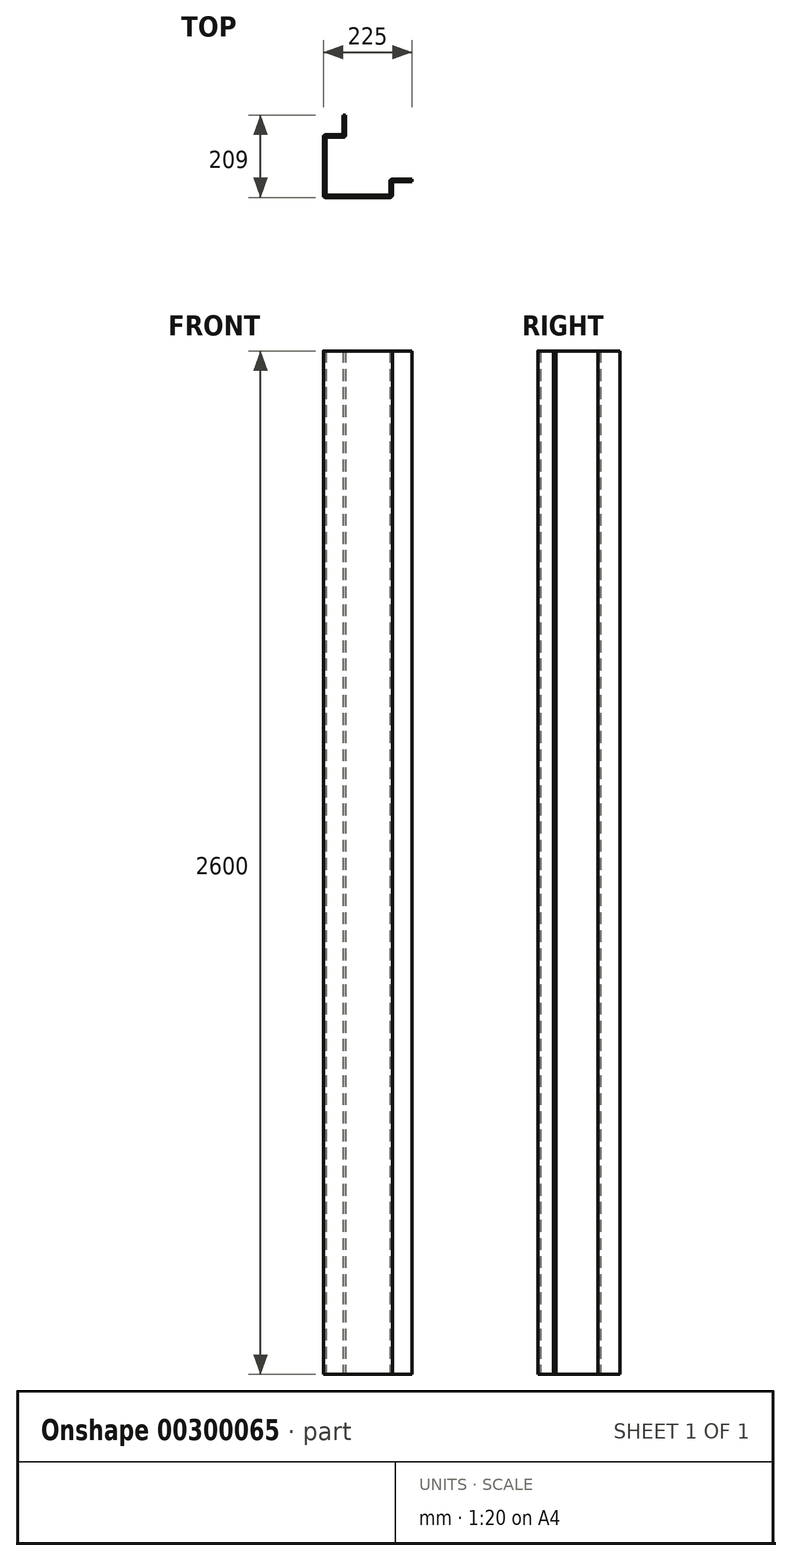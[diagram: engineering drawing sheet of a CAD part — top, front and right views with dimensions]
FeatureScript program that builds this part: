
annotation { "Feature Type Name" : "Feature", "Feature Type Description" : "" }
export const myFeature = defineFeature(function(context is Context, id is Id, definition is map)
    precondition{}
    {
        {
            var Q0;
            Q0=qCreatedBy(makeId("Top.planeOp"),FACE);
            var sketch = newSketch(context, id + "F0", { "sketchPlane" : qUnion([Q0])});
            skLineSegment(sketch, "E0", {"start": v(0, 0) * mm, "end": v(-45, 0) * mm});
            skLineSegment(sketch, "E1", {"start": v(-50, -5) * mm, "end": v(-50, -35) * mm});
            skLineSegment(sketch, "E2", {"start": v(-55, -40) * mm, "end": v(-220, -40) * mm});
            skLineSegment(sketch, "E3", {"start": v(-225, -35) * mm, "end": v(-225, 114) * mm});
            skLineSegment(sketch, "E4", {"start": v(-220, 119) * mm, "end": v(-180, 119) * mm});
            skLineSegment(sketch, "E5", {"start": v(-175, 124) * mm, "end": v(-175, 169) * mm});
            skLineSegment(sketch, "E6", {"start": v(-175, 169) * mm, "end": v(-169, 169) * mm});
            skLineSegment(sketch, "E7", {"start": v(-169, 169) * mm, "end": v(-169, 118) * mm});
            skLineSegment(sketch, "E8", {"start": v(-174, 113) * mm, "end": v(-214, 113) * mm});
            skLineSegment(sketch, "E9", {"start": v(-219, 108) * mm, "end": v(-219, -29) * mm});
            skLineSegment(sketch, "E10", {"start": v(-214, -34) * mm, "end": v(-61, -34) * mm});
            skLineSegment(sketch, "E11", {"start": v(-56, -29) * mm, "end": v(-56, 1) * mm});
            skLineSegment(sketch, "E12", {"start": v(-51, 6) * mm, "end": v(0, 6) * mm});
            skLineSegment(sketch, "E13", {"start": v(0, 6) * mm, "end": v(0, 0) * mm});
            skPoint(sketch, "E14.visualSharp", {"position": v(-225, -40) * mm});
            skArc(sketch, "E14.filletArc", {"start": v(-225, -35) * mm, "mid": v(-223.54, -38.54) * mm, "end": v(-220, -40) * mm});
            skPoint(sketch, "E15.visualSharp", {"position": v(-219, -34) * mm});
            skArc(sketch, "E15.filletArc", {"start": v(-219, -29) * mm, "mid": v(-217.54, -32.54) * mm, "end": v(-214, -34) * mm});
            skPoint(sketch, "E16.visualSharp", {"position": v(-56, -34) * mm});
            skArc(sketch, "E16.filletArc", {"start": v(-61, -34) * mm, "mid": v(-57.46, -32.54) * mm, "end": v(-56, -29) * mm});
            skPoint(sketch, "E17.visualSharp", {"position": v(-56, 6) * mm});
            skArc(sketch, "E17.filletArc", {"start": v(-51, 6) * mm, "mid": v(-54.54, 4.54) * mm, "end": v(-56, 1) * mm});
            skPoint(sketch, "E18.visualSharp", {"position": v(-50, 0) * mm});
            skArc(sketch, "E18.filletArc", {"start": v(-45, 0) * mm, "mid": v(-48.54, -1.46) * mm, "end": v(-50, -5) * mm});
            skPoint(sketch, "E19.visualSharp", {"position": v(-175, 119) * mm});
            skArc(sketch, "E19.filletArc", {"start": v(-180, 119) * mm, "mid": v(-176.46, 120.46) * mm, "end": v(-175, 124) * mm});
            skPoint(sketch, "E20.visualSharp", {"position": v(-169, 113) * mm});
            skArc(sketch, "E20.filletArc", {"start": v(-174, 113) * mm, "mid": v(-170.46, 114.46) * mm, "end": v(-169, 118) * mm});
            skPoint(sketch, "E21.visualSharp", {"position": v(-225, 119) * mm});
            skArc(sketch, "E21.filletArc", {"start": v(-220, 119) * mm, "mid": v(-223.54, 117.54) * mm, "end": v(-225, 114) * mm});
            skPoint(sketch, "E22.visualSharp", {"position": v(-219, 113) * mm});
            skArc(sketch, "E22.filletArc", {"start": v(-214, 113) * mm, "mid": v(-217.54, 111.54) * mm, "end": v(-219, 108) * mm});
            skPoint(sketch, "E23.visualSharp", {"position": v(-50, -40) * mm});
            skArc(sketch, "E23.filletArc", {"start": v(-55, -40) * mm, "mid": v(-51.46, -38.54) * mm, "end": v(-50, -35) * mm});
            skSolve(sketch);
        }
        {
            var Q0;
            Q0 = qSketchRegion(id + "F0", true);
            extrude(context, id + "F1", {"entities" : qUnion([Q0]), "depth" : 2600 * mm});
        }
    });
